# Revit family: DCST_Счетчик тепла ультразвуковой_СТК МАРС NEO У
name_source: partatom
category: Арматура трубопроводов
units: mm (PartAtom-declared; Revit-internal decimal feet)

## family parameters
Всегда вертикально = Да
На основе рабочей плоскости = Нет
Общий = Нет
При загрузке вырезать с полостями = Нет
Размер круглого соединителя = Использовать диаметр
Тип детали = Вставляется

## types (4) — shared parameters
ADSK_Единица измерения = шт.
ADSK_Завод-изготовитель = Декаст
ADSK_Количество = 1
D = 25 мм
IV = ♦ : импульсный выход (открытый коллектор) — только для подачи Ду15
LT = СТК МАРС NEO У
MB = ♦ : M-Bus
RS = ♦ : RS-485 (протокол M-Bus)
RS4 = ♦ : RS-485 (протокол M-Bus) + 4 имп.
URL = https://www.decast.com
s = 90 мм
w = 116 мм
Изготовитель = Декаст

## per-type parameters (varying)
| type | ADSK_Диаметр условный | Диаметр условного прохода | Диаметр штуцера | Длина гаек | Длина штуцера | Монтажная длина | Обратная магистраль | Размер под ключ | УГО_Высота | УГО_Длина | УГО_Длина линии |
| СТК МАРС NEO-15 У Подача | 15 мм | 15 мм | 18 мм | 14 мм | 40 мм | 110 мм | Нет | 30 мм | 55 мм | 110 мм | 40 мм |
| СТК МАРС NEO-15 У Обратка | 15 мм | 15 мм | 18 мм | 14 мм | 40 мм | 110 мм | Да | 30 мм | 55 мм | 110 мм | 40 мм |
| СТК МАРС NEO-20 У Подача | 20 мм | 20 мм | 25 мм | 17 мм | 50 мм | 130 мм | Нет | 35 мм | 65 мм | 130 мм | 50 мм |
| СТК МАРС NEO-20 У Обратка | 20 мм | 20 мм | 25 мм | 17 мм | 50 мм | 130 мм | Да | 35 мм | 65 мм | 130 мм | 50 мм |
